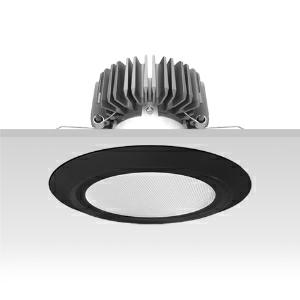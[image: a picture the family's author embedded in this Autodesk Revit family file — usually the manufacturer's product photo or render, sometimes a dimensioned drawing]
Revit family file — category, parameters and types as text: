
# Revit family: 3f_filippi_-_3f_reno_bianco_ampio_3f_filippi_-_30683_a01038_-_3f_reno_200_wh_3000-930_dali_wide___vs_bk_ac82
name_source: partatom
category: Lighting Fixtures
units: mm (PartAtom-declared; Revit-internal decimal feet)

## family parameters
Cut with Voids When Loaded = No
Host = Face
Light Source = No
Part Type = Normal
Room Calculation Point = No
Round Connector Dimension = Use Diameter
Shared = No

## types (1)
- 3F Filippi - 3F Reno Bianco Ampio (1 x LED, 2320 lm, 37 W, 3000 K)
    Apparent Load = 37 VA
    Approval mark = CE
    CIE Flux Codes = 75 94 99 100 100
    Color Rendering = 90
    Color Temperature = 3000 K
    Control Gear = Electronic transformer
    Default Elevation = 1800 mm
    Description = ILLUMINOTECHNICAL
Luminous efficiency 100% (DLOR 100%, ULOR 0%).
Initial luminous flux of the luminaire 2320 lm.
Direct symmetric wide distribution.
Installation Interdistance Transv.D = 1.16 x hu - Long.D = 1.14 x hu.
Tabular UGR (CIE 117 - 4H-8H; S=0.25H; 70/50/20): RUG 21.5 - 21.4.
Beam angle: 74° - 74°.
Luminous efficacy 63 lm/W.
Lifetime (L90/B10): 30000 h. (tq+25°C)
Lifetime (L85/B10): 50000 h. (tq+25°C)
Lifetime (L70/B10): 80000 h. (tq+25°C)
Sudden decreased luminous flux after 50000 hours: 0% (C0).
Photobiological safety in compliance with IEC/TR 62778: RG0 risk exempt, (IEC 62471).
In compliance with IEC/EN 62722-2-1 - IEC/EN 62717 standards.

SOURCE
Compact LED module 3000/930.
Energy efficiency class (UE 2019/2020 - UE 2019/2015): E.
CIE 13.3 Colour rendering index: CRI >90 (R9 >50%).
IES TM-30 Fidelity Index: Rf = 92 Rg = 101.
CCT nominal colour temperature 3000 K.
Colour initial tolerance (MacAdam): SDCM 3.
Zhaga Book 3 compliant.

MECHANICAL
Passive heat dissipator in die-casting aluminium, oversized, for optimum thermal management of the LED module.
Parabolic element with graduated/concentric rings in white polycarbonate.
Transparent external lens with glossy and satin differentiated surfaces, with a cooling and anti-insect system in methacrylate (PMMA).
Fastening spring clips in stainless steel.
Dimensions: diameter 226 mm, height 146 mm. Weight 1.825 kg.
IP44 protection degree for exposed part, IP20 for recessed part.
Mechanical strength to impacts IK06 (1 joule).
Glow-wire test resistance 650°C.

ELECTRICAL
Wiring on a separate unit.
Halogen Free DALI-2 DATI (Parts 251, 252, 253), PUSH-DIM, electronic wiring 230V-50/60Hz, power factor 0.97 at full load, THD <25%, constant output current, SELV, class II, 1 driver, 1 DALI addresse.
Power of the luminaire 37 W.
ENEC - CE.
SAFE FLICKER: PstLM=<1 and SVM=<0.4 (IEC TR 61547-1 and IEC TR 63158), to ensure a more comfortable and safe light.
Luminaire compliant with EN 60598-2-22 for power supply from a centralised emergency system CPSS (Central Power Supply System), not incorporated in the luminaire - high risk areas excluded. The default power and flux are 100% in AC and 100% in DC.
Ambient temperature from 0°C to +25°C.
Temperature class T6 max 85°C.
Relative humidity UR: <85%.

INSTALLATION
Pull-up recessed fitting.
False ceiling carving: 200 mm.
All accessories dedicated to this product are available on the Catalog and on our website www.3F-Filippi.com.

ACCESSORIES
A01038 - Anti-glare microprismatic VS moulded glass, tempered, not flammable, locked and in line with the trim, in black polycarbonate.

APPLICATIONS
Environments: architectural, commercial, exhibition areas, transit areas, corridors, shops, display windows, service areas.
In false ceilings with narrow voids.

LIGHT MANAGEMENT
Recommended minimum setting: 10%.
The luminaire, equipped with (DALI-2 DATI) driver, can be controlled manually with 3F Easy Dim technology or automatically/manually with wired or wireless DALI/D2D control systems.
The D2D driver guarantees interoperability with other devices with the same certification by making the following information available:
Device Data (Part 251), Energy Report (Part 252), Diagnosis & Maintenance (Part 253).
In electrical systems without a regulation system (manual or automatic) and DALI bus, a suitable jumper must be made on the DA-DA terminals of the appliance.

WARNING
Luminaire designed for disposal/recycling at end-of-life.
Replaceable (LED only) light source by a professional. Replaceable control gear by a professional.
    Height = 0 mm  [stored 0 ft]
    Lamp = 1 x LED
    Lamp Light Flux = 2320 lm
    Lamp Power = 37 W
    Lamp count = 1
    Length = 226 mm
    Lifetime = 50000 h
    Luminous efficacy = 63 lm/W
    Manufacturer = 3F Filippi
    ModVariant = No
    Model = 3F Filippi - 30683+A01038 - 3F Reno 200 WH 3000-930 DALI WIDE + VS BK
    Mounting Place = Ceiling
    Mounting Type = Recessed
    Number of Poles = 1
    OnlyDefault = Yes
    Power Factor = 1
    Product Name = 3F Filippi - 3F Reno Bianco Ampio
    Product group = recessed luminaire
    ProductGroupID = 4
    Protection Class = Protection class II
    Protection Degree = IP 20
    RLX_Detail_Level = 1
    RLX_Emergency_Light_Flux = 0 lm
    RLX_Emergency_Type = 0
    RLX_Emergency_Type_DB = No
    RlxData = <blob elided: 98449 chars, md5=22d7799f>
    Socket = socket
    Standby Power = 0 W
    System Light Flux = 2320 lm
    System Power = 37 W
    Type Comments = Product without accessories
    Type Image = 3ffilippi_3f_reno_200_bk_vs_smp.jpg
    URL = http://relux.com
    VarID = ---
    Voltage = 0 V
    Weight = 0.00 kg
    Width = 0 mm  [stored 0 ft]

note: [stored X ft] marks values corroborated as IEEE doubles in the binary element streams (Revit-internal decimal feet)

## geometry (parser evidence)
native form markers: Blend x4, Sweep x11
no freeform markers — native parametric forms only
